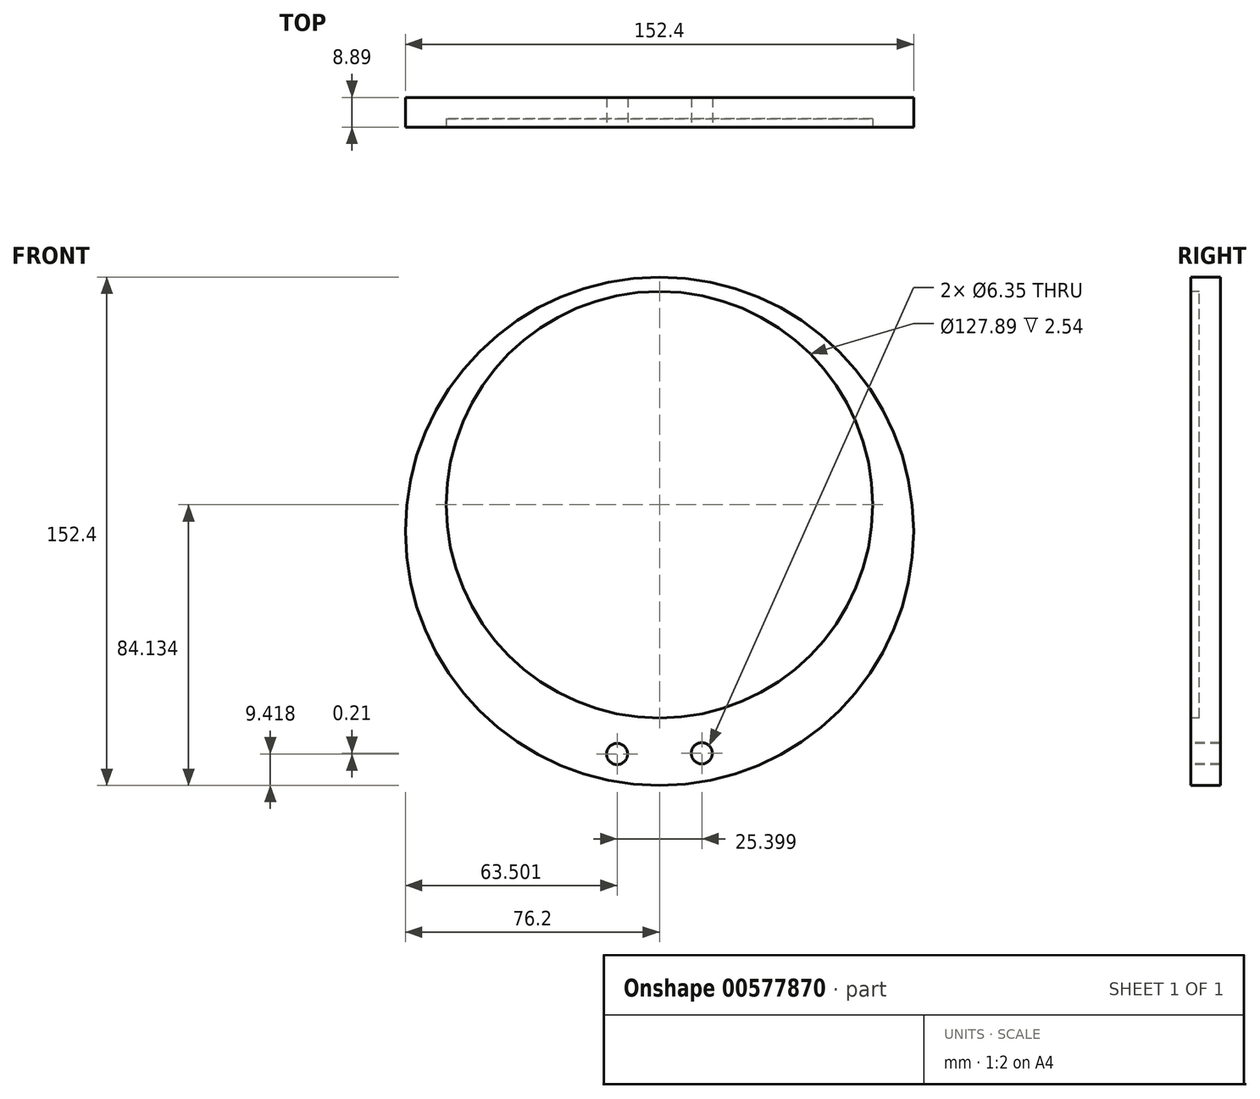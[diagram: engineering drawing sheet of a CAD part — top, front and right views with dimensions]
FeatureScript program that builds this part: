
annotation { "Feature Type Name" : "Feature", "Feature Type Description" : "" }
export const myFeature = defineFeature(function(context is Context, id is Id, definition is map)
    precondition{}
    {
        {
            var Q0;
            Q0=qCreatedBy(makeId("Front.planeOp"),FACE);
            var sketch = newSketch(context, id + "F0", { "sketchPlane" : qUnion([Q0])});
            skCircle(sketch, "E0", {"center": v(0, 0) * mm, "radius": 76.2 * mm});
            skSolve(sketch);
        }
        {
            var Q0;
            Q0 = qSketchRegion(id + "F0", true);
            extrude(context, id + "F1", {"entities" : qUnion([Q0]), "depth" : 8.9 * mm, "offsetDistance" : 25.4 * mm});
        }
        {
            var Q0;
            Q0=makeQuery(id+"F1.opExtrude","CAP_FACE",FACE,{"disambiguationData":[OSD([sQuery(id+"F0.wireOp",EDGE,"E0")])],"isStart":false});
            var sketch = newSketch(context, id + "F2", { "sketchPlane" : qUnion([Q0])});
            skCircle(sketch, "E1", {"center": v(0, 7.93) * mm, "radius": 63.94 * mm});
            skSolve(sketch);
        }
        {
            var Q0;
            Q0=makeQuery(id+"F2.imprint","IMPRINT",FACE,{"disambiguationData":[TD([[makeQuery(id+"F2.imprint","IMPRINT",EDGE,{"derivedFrom":sQuery(id+"F2.wireOp",EDGE,"E1")}),1.0]])]});
            extrude(context, id + "F3", {"entities" : qUnion([Q0]), "operationType" : NewBodyOperationType.REMOVE, "oppositeDirection" : true, "depth" : 2.54 * mm, "offsetDistance" : 25.4 * mm});
        }
        {
            var Q0;
            Q0=makeQuery(id+"F1.opExtrude","CAP_FACE",FACE,{"disambiguationData":[OSD([sQuery(id+"F0.wireOp",EDGE,"E0")])],"isStart":false});
            var sketch = newSketch(context, id + "F4", { "sketchPlane" : qUnion([Q0])});
            skPoint(sketch, "E2", {"position": v(-12.7, -66.78) * mm});
            skPoint(sketch, "E3", {"position": v(12.7, -66.57) * mm});
            skLineSegment(sketch, "E4", {"start": v(-12.7, -66.78) * mm, "end": v(12.7, -66.57) * mm});
            skSolve(sketch);
        }
        {
            var Q0;
            Q0=sQuery(id+"F4.wireOp",VERTEX,"E2");
            var Q1;
            Q1=sQuery(id+"F4.wireOp",VERTEX,"E3");
            var Q2;
            Q2=makeQuery(id+"F1.opExtrude","SWEPT_BODY",BODY,{"disambiguationData":[OSD([sQuery(id+"F0.wireOp",EDGE,"E0")])]});
            hole(context, id + "F5", {"style" : HoleStyle.SIMPLE, "endStyle" : HoleEndStyle.THROUGH, "holeDiameter" : 6.35 * mm, "isTappedThrough" : true, "tappedDepth" : 12.7 * mm, "tapClearance" : 3, "locations" : qUnion([Q0, Q1]), "scope" : qUnion([Q2])});
        }
    });
